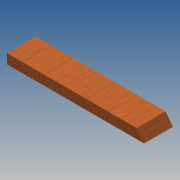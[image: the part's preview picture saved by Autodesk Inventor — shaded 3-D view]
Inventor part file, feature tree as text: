
AUTODESK INVENTOR PART (.ipt)
format: ipt  version: 2014 SP1 (Build 180222100, 222)  size: 94,208 bytes
history: native  units: in
note: dims shown in document units (in); Inventor stores cm internally (conversion verified against a paired STEP export)
features: extrude x2, sketch x2
ambient origin geometry x8: Origin, YZ Plane, XZ Plane, XY Plane, X Axis, Y Axis, Z Axis, Center Point
bodies: Solid1 (feature_tree)
feature tree (4):
  extrude  "Extrusion1"  Depth=1.4961in
  extrude  "Extrusion2"  Depth=4.4882in TaperAngle=0.0deg
  sketch  "Sketch1"  dims[d0=21.3386in d1=1.4961in]
  sketch  "Sketch3"  dims[d2=0.3573in d3=4.4882in d4=0.0in d21=1.4961in d22=0.5906in d23=0.0394in d24=0.0in]
